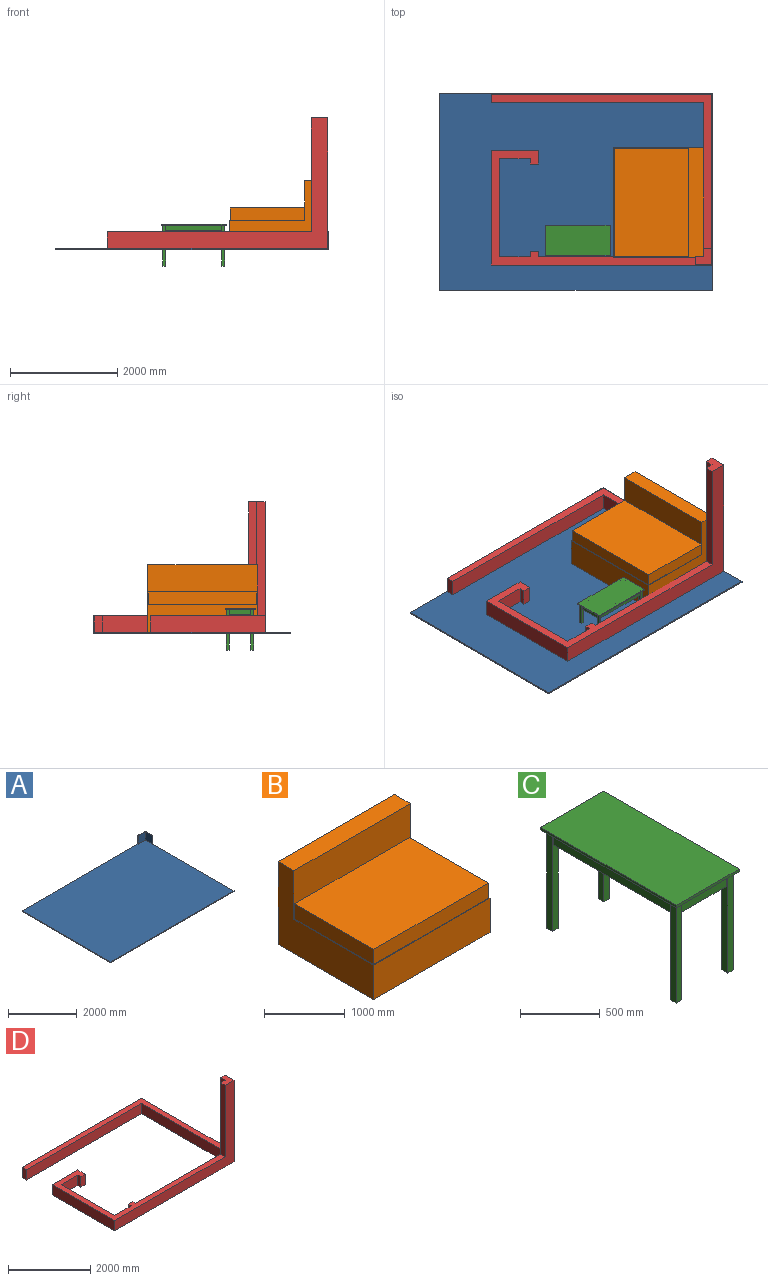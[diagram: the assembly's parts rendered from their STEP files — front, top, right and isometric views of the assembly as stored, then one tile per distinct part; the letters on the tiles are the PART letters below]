
ASSEMBLY  parts=4 mates=5
PART A: 11 faces, bbox 5080x3657.6x330.2 mm
  f0: plane 5080x330.2mm, normal (0,1,0), area 221935mm2, adj f1,f3,f4,f5,f6,f10
  f1: plane 3657.6x25.4mm, normal (-1,0,0), area 92903mm2, adj f0,f2,f4,f5
  f2: plane 5080x25.4mm, normal (0,-1,0), area 129032mm2, adj f1,f3,f4,f5
  f3: plane 3657.6x330.2mm, normal (1,0,0), area 185806.1mm2, adj f0,f2,f4,f5,f9,f10
  f4: plane 5080x3657.6mm, normal (0,0,1), area 18573027.4mm2, adj f0,f1,f2,f3,f6,f7,f8,f9
  f5: plane 5080x3657.6mm, normal (0,0,-1), area 18580608mm2, adj f0,f1,f2,f3
  f6: plane 304.8x12.7mm, normal (-1,0,0), area 3871mm2, adj f0,f4,f7,f10
  f7: plane 304.8x292.1mm, normal (0,-1,0), area 89032.1mm2, adj f4,f6,f8,f10
  f8: plane 304.8x292.1mm, normal (-1,0,0), area 89032.1mm2, adj f4,f7,f9,f10
  f9: plane 304.8x12.7mm, normal (0,-1,0), area 3871mm2, adj f3,f4,f8,f10
  f10: plane 304.8x304.8mm, normal (0,0,1), area 7580.6mm2, adj f0,f3,f6,f7,f8,f9
PART B: 12 faces, bbox 2038.4x1676.4x1257.3 mm
  f0: plane 1676.4x1257.3mm, normal (-1,0,0), area 1078707.5mm2, adj f1,f2,f3,f5,f6,f7
  f1: plane 2038.35x520.7mm, normal (0,-1,0), area 1061368.8mm2, adj f0,f4,f5,f6
  f2: plane 2038.35x279.4mm, normal (0,0,1), area 569515mm2, adj f0,f3,f4,f7
  f3: plane 2038.35x1257.3mm, normal (0,1,0), area 2562817.5mm2, adj f0,f2,f4,f5
  f4: plane 1676.4x1257.3mm, normal (1,0,0), area 1078707.5mm2, adj f1,f2,f3,f5,f6,f7
  f5: plane 2038.35x1676.4mm, normal (0,0,-1), area 3417089.9mm2, adj f0,f1,f3,f4
  f6: plane 2038.35x1397mm, normal (0,0,1), area 61048.3mm2, adj f0,f1,f4,f7,f8,f9,f10
  f7: plane 2038.35x736.6mm, normal (0,-1,0), area 1041288.2mm2, adj f0,f2,f4,f6,f8,f10,f11
  f8: plane 1384.3x228.6mm, normal (-1,0,0), area 316451mm2, adj f6,f7,f9,f11
  f9: plane 2012.95x228.6mm, normal (0,-1,0), area 460160.4mm2, adj f6,f8,f10,f11
  f10: plane 1384.3x228.6mm, normal (1,0,0), area 316451mm2, adj f6,f7,f9,f11
  f11: plane 2012.95x1384.3mm, normal (0,0,1), area 2786526.7mm2, adj f7,f8,f9,f10
PART C: 39 faces, bbox 558.8x1200.2x774.7 mm
  f0: plane 1200.15x558.8mm, normal (0,0,-1), area 123709.4mm2, adj f2,f3,f4,f5,f7,f10,f13,f16
  f1: plane 1073.15x431.8mm, normal (0,0,-1), area 462741mm2, adj f8,f11,f14,f17,f19,f22,f24,f25
  f2: plane 558.8x19.05mm, normal (0,1,0), area 10645.1mm2, adj f0,f3,f5,f6
  f3: plane 1200.15x19.05mm, normal (-1,0,0), area 22862.9mm2, adj f0,f2,f4,f6
  f4: plane 558.8x19.05mm, normal (0,-1,0), area 10645.1mm2, adj f0,f3,f5,f6
  f5: plane 1200.15x19.05mm, normal (1,0,0), area 22862.9mm2, adj f0,f2,f4,f6
  f6: plane 1200.15x558.8mm, normal (0,0,1), area 670643.8mm2, adj f2,f3,f4,f5
  f7: plane 1047.75x95.25mm, normal (-1,0,0), area 99798.2mm2, adj f0,f9,f25,f34
  f8: plane 1047.75x95.25mm, normal (1,0,0), area 99798.2mm2, adj f1,f9,f25,f34
  f9: plane 1047.75x25.4mm, normal (0,0,-1), area 26612.9mm2, adj f7,f8,f25,f34
  f10: plane 406.4x95.25mm, normal (0,-1,0), area 38709.6mm2, adj f0,f12,f22,f24
  f11: plane 406.4x95.25mm, normal (0,1,0), area 38709.6mm2, adj f1,f12,f22,f24
  f12: plane 406.4x25.4mm, normal (0,0,-1), area 10322.6mm2, adj f10,f11,f22,f24
  f13: plane 1047.75x95.25mm, normal (1,0,0), area 99798.2mm2, adj f0,f15,f19,f32
  f14: plane 1047.75x95.25mm, normal (-1,0,0), area 99798.2mm2, adj f1,f15,f19,f32
  f15: plane 1047.75x25.4mm, normal (0,0,-1), area 26612.8mm2, adj f13,f14,f19,f32
  f16: plane 406.4x95.25mm, normal (0,1,0), area 38709.6mm2, adj f0,f18,f29,f37
  f17: plane 406.4x95.25mm, normal (0,-1,0), area 38709.6mm2, adj f1,f18,f29,f37
  f18: plane 406.4x25.4mm, normal (0,0,-1), area 10322.6mm2, adj f16,f17,f29,f37
  f19: plane 755.65x50.8mm, normal (0,1,0), area 35967.7mm2, adj f0,f1,f13,f14,f15,f20,f22,f23
  f20: plane 755.65x50.8mm, normal (1,0,0), area 38387mm2, adj f0,f19,f21,f23
  f21: plane 755.65x50.8mm, normal (0,-1,0), area 38387mm2, adj f0,f20,f22,f23
  f22: plane 755.65x50.8mm, normal (-1,0,0), area 35967.7mm2, adj f0,f1,f10,f11,f12,f19,f21,f23
  f23: plane 50.8x50.8mm, normal (0,0,-1), area 2580.6mm2, adj f19,f20,f21,f22
  f24: plane 755.65x50.8mm, normal (1,0,0), area 35967.7mm2, adj f0,f1,f10,f11,f12,f25,f26,f28
  f25: plane 755.65x50.8mm, normal (0,1,0), area 35967.7mm2, adj f0,f1,f7,f8,f9,f24,f27,f28
  f26: plane 755.65x50.8mm, normal (0,-1,0), area 38387mm2, adj f0,f24,f27,f28
  f27: plane 755.65x50.8mm, normal (-1,0,0), area 38387mm2, adj f0,f25,f26,f28
  f28: plane 50.8x50.8mm, normal (0,0,-1), area 2580.6mm2, adj f24,f25,f26,f27
  f29: plane 755.65x50.8mm, normal (-1,0,0), area 35967.7mm2, adj f0,f1,f16,f17,f18,f30,f32,f33
  f30: plane 755.65x50.8mm, normal (0,1,0), area 38387mm2, adj f0,f29,f31,f33
  f31: plane 755.65x50.8mm, normal (1,0,0), area 38387mm2, adj f0,f30,f32,f33
  f32: plane 755.65x50.8mm, normal (0,-1,0), area 35967.7mm2, adj f0,f1,f13,f14,f15,f29,f31,f33
  f33: plane 50.8x50.8mm, normal (0,0,-1), area 2580.6mm2, adj f29,f30,f31,f32
  f34: plane 755.65x50.8mm, normal (0,-1,0), area 35967.7mm2, adj f0,f1,f7,f8,f9,f35,f37,f38
  f35: plane 755.65x50.8mm, normal (-1,0,0), area 38387mm2, adj f0,f34,f36,f38
  f36: plane 755.65x50.8mm, normal (0,1,0), area 38387mm2, adj f0,f35,f37,f38
  f37: plane 755.65x50.8mm, normal (1,0,0), area 35967.7mm2, adj f0,f1,f16,f17,f18,f34,f36,f38
  f38: plane 50.8x50.8mm, normal (0,0,-1), area 2580.6mm2, adj f34,f35,f36,f37
PART D: 24 faces, bbox 4102.1x3175x2425.7 mm
  f0: plane 3797.3x2133.6mm, normal (0,0,1), area 1021933.4mm2, adj f1,f2,f3,f4,f5,f6,f7,f8
  f1: plane 304.8x101.6mm, normal (-1,0,0), area 30967.7mm2, adj f0,f2,f18,f20
  f2: plane 571.5x304.8mm, normal (0,1,0), area 174193.2mm2, adj f0,f1,f3,f20
  f3: plane 1828.8x304.8mm, normal (1,0,0), area 557418.2mm2, adj f0,f2,f4,f20
  f4: plane 571.5x304.8mm, normal (0,-1,0), area 174193.2mm2, adj f0,f3,f5,f20
  f5: plane 304.8x101.6mm, normal (-1,0,0), area 30967.7mm2, adj f0,f4,f6,f20
  f6: plane 304.8x152.4mm, normal (0,-1,0), area 46451.5mm2, adj f0,f5,f7,f20
  f7: plane 304.8x254mm, normal (1,0,0), area 77419.2mm2, adj f0,f6,f8,f20
  f8: plane 876.3x304.8mm, normal (0,1,0), area 267096.2mm2, adj f0,f7,f9,f20
  f9: plane 2133.6x304.8mm, normal (-1,0,0), area 650321.3mm2, adj f0,f8,f10,f20
  f10: plane 4102.1x2425.7mm, normal (0,-1,0), area 1896770.4mm2, adj f0,f9,f11,f20,f21,f23
  f11: plane 3175x2425.7mm, normal (1,0,0), area 1614190.3mm2, adj f10,f12,f19,f20,f22,f23
  f12: plane 4102.1x304.8mm, normal (0,1,0), area 1250320.1mm2, adj f11,f13,f19,f20
  f13: plane 304.8x152.4mm, normal (-1,0,0), area 46451.5mm2, adj f12,f14,f19,f20
  f14: plane 3949.7x304.8mm, normal (0,-1,0), area 1203868.6mm2, adj f13,f15,f19,f20
  f15: plane 2870.2x2425.7mm, normal (-1,0,0), area 1198062.1mm2, adj f14,f16,f19,f20,f22,f23
  f16: plane 3073.4x2425.7mm, normal (0,1,0), area 1259997.5mm2, adj f0,f15,f17,f20,f21,f23
  f17: plane 304.8x101.6mm, normal (1,0,0), area 30967.7mm2, adj f0,f16,f18,f20
  f18: plane 304.8x152.4mm, normal (0,1,0), area 46451.5mm2, adj f0,f1,f17,f20
  f19: plane 4102.1x2870.2mm, normal (0,0,1), area 1039352.8mm2, adj f11,f12,f13,f14,f15,f22
  f20: plane 4102.1x3175mm, normal (0,0,-1), area 2130963.5mm2, adj f1,f2,f3,f4,f5,f6,f7,f8
  f21: plane 2120.9x152.4mm, normal (-1,0,0), area 323225.2mm2, adj f0,f10,f16,f23
  f22: plane 2120.9x152.4mm, normal (0,1,0), area 323225.2mm2, adj f11,f15,f19,f23
  f23: plane 304.8x304.8mm, normal (0,0,1), area 69677.3mm2, adj f10,f11,f15,f16,f21,f22
PLACE A t=(3401.35,268.95,-449.15)mm
PLACE B rot(axis=(0,0,-1),90deg) t=(8494.85,4491.63,-423.75)mm
PLACE C rot(axis=(0,0,-1),90deg) t=(5520.34,3932.84,0)mm
PLACE D t=(-440.91,-1054.1,-423.75)mm
MATE planar A.f4 <-> D.f20  axis (0,0,1) through (5907.66,4785.75,-423.75)mm
MATE planar B.f5 <-> A.f4  axis (0,0,-1) through (7445.37,4588.62,-423.75)mm
MATE planar B.f3 <-> D.f15  axis (1,0,0) through (8283.57,4588.62,204.9)mm
MATE planar A.f7 <-> D.f12  axis (0,-1,0) through (8289.92,6602.56,-271.35)mm
MATE planar A.f8 <-> D.f11  axis (-1,0,0) through (8435.97,6456.51,-271.35)mm
